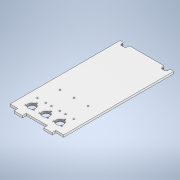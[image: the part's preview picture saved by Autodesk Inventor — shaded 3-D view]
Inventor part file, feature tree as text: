
AUTODESK INVENTOR PART (.ipt)
format: ipt  version: 2020 (Build 240168000, 168)  size: 218,112 bytes
history: native  units: mm
features: extrude x4, sketch x4, pattern_linear x3
ambient origin geometry x8: Origin, YZ Plane, XZ Plane, XY Plane, X Axis, Y Axis, Z Axis, Center Point
bodies: Solid1 (feature_tree)
feature tree (11):
  extrude  "base"  Depth=3.0mm
  extrude  "Poke Hole"  Depth=3.0mm
  pattern_linear  "Rectangular Pattern1"  Spacing1=9.0mm  [1 undecoded]
  extrude  "Mount Holes"  Depth=19.7mm
  pattern_linear  "Rectangular Pattern2"  Spacing1=1.5mm  [1 undecoded]
  extrude  "PCB mount holes"  Depth=126.0mm
  pattern_linear  "Rectangular Pattern3"  Spacing1=18.25mm  [1 undecoded]
  sketch  "Sketch1"  dims[d3=12.7mm d5=3.0mm]
  sketch  "Sketch2"  dims[d7=12.7mm d9=3.0mm]
  sketch  "Sketch3"  dims[d10=9.0mm]
  sketch  "Sketch4"  dims[d11=19.7mm d13=9.0mm d14=19.7mm d16=1.5mm d17=126.0mm d20=18.25mm d21=18.25mm d22=57.15mm d23=9.0mm d24=9.0mm d27=250.0mm d28=250.0mm d29=5.0mm d30=0.0mm d31=18.0mm d32=21.5mm d33=5.0mm d34=0.0mm d35=20.0mm d37=33.0mm d38=20.0mm d40=33.0mm d41=3.0mm d42=11.1mm d43=30.0mm d45=360.0deg d47=5.0mm d48=0.0mm d49=30.0mm d51=33.0mm d52=33.0mm d53=83.0mm d54=3.7mm d55=3.3mm d56=3.3mm d57=19.75mm d58=3.3mm d59=44.5mm d61=11.5mm d62=10.0mm d63=0.0mm d64=30.0mm d66=33.0mm]
note: 3 required parameter values undecoded (feature->parameter linkage not recoverable at this tier; creation-order binding heuristic only, values carry confidence <= 0.55)
